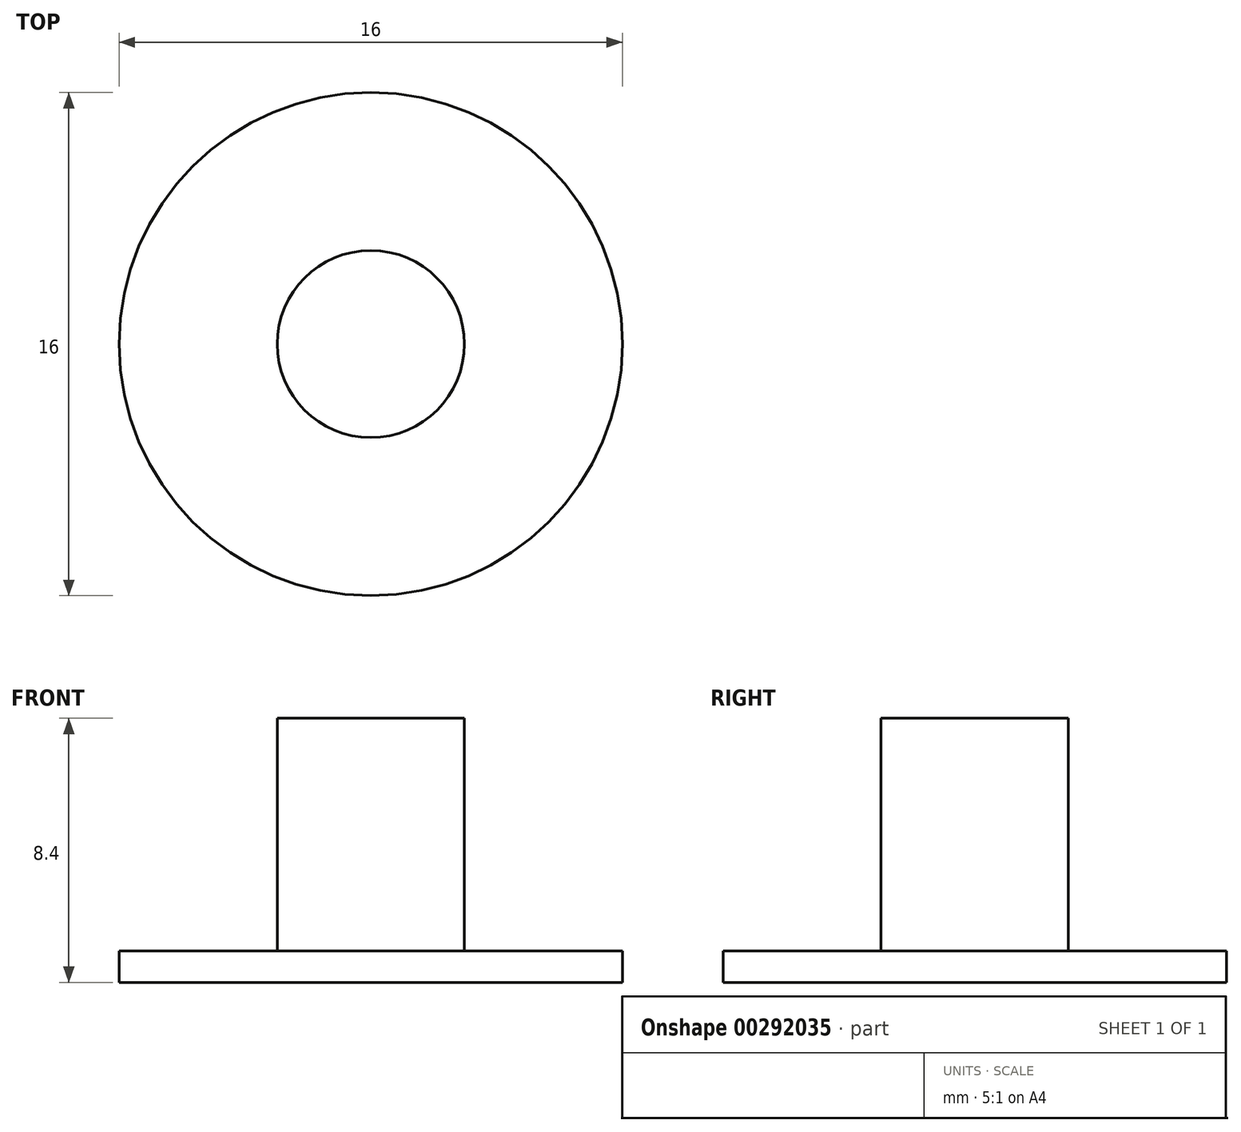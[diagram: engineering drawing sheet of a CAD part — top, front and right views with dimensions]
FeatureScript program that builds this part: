
annotation { "Feature Type Name" : "Feature", "Feature Type Description" : "" }
export const myFeature = defineFeature(function(context is Context, id is Id, definition is map)
    precondition{}
    {
        {
            var Q0;
            Q0=qCreatedBy(makeId("Top.planeOp"),FACE);
            var sketch = newSketch(context, id + "F0", { "sketchPlane" : qUnion([Q0])});
            skCircle(sketch, "E0", {"center": v(-0.16, 0.89) * mm, "radius": 8 * mm});
            skPoint(sketch, "E0.first.point", {"position": v(-4.05, 7.88) * mm});
            skPoint(sketch, "E0.second.point", {"position": v(5.58, -4.68) * mm});
            skPoint(sketch, "E0.third.point", {"position": v(4, -5.94) * mm});
            skSolve(sketch);
        }
        {
            var Q0;
            Q0 = qSketchRegion(id + "F0", true);
            extrude(context, id + "F1", {"entities" : qUnion([Q0]), "depth" : 1 * mm});
        }
        {
            var Q0;
            Q0=makeQuery(id+"F1.opExtrude","SWEPT_BODY",BODY,{"disambiguationData":[OSD([sQuery(id+"F0.wireOp",EDGE,"E0")])]});
            deleteBodies(context, id + "F2", {"entities" : qUnion([Q0])});
        }
        {
            var Q0;
            Q0=qCreatedBy(makeId("Top.planeOp"),FACE);
            var sketch = newSketch(context, id + "F3", { "sketchPlane" : qUnion([Q0])});
            skCircle(sketch, "E1", {"center": v(0, 0) * mm, "radius": 8 * mm});
            skSolve(sketch);
        }
        {
            var Q0;
            Q0 = qSketchRegion(id + "F3", true);
            extrude(context, id + "F4", {"entities" : qUnion([Q0]), "depth" : 1 * mm});
        }
        {
            var Q0;
            Q0=makeQuery(id+"F4.opExtrude","CAP_FACE",FACE,{"disambiguationData":[OSD([sQuery(id+"F3.wireOp",EDGE,"E1")])],"isStart":false});
            var sketch = newSketch(context, id + "F5", { "sketchPlane" : qUnion([Q0])});
            skCircle(sketch, "E2", {"center": v(0, 0) * mm, "radius": 2.98 * mm});
            skSolve(sketch);
        }
        {
            var Q0;
            Q0 = qSketchRegion(id + "F5", true);
            extrude(context, id + "F6", {"entities" : qUnion([Q0]), "operationType" : NewBodyOperationType.ADD, "depth" : 7.4 * mm});
        }
    });
